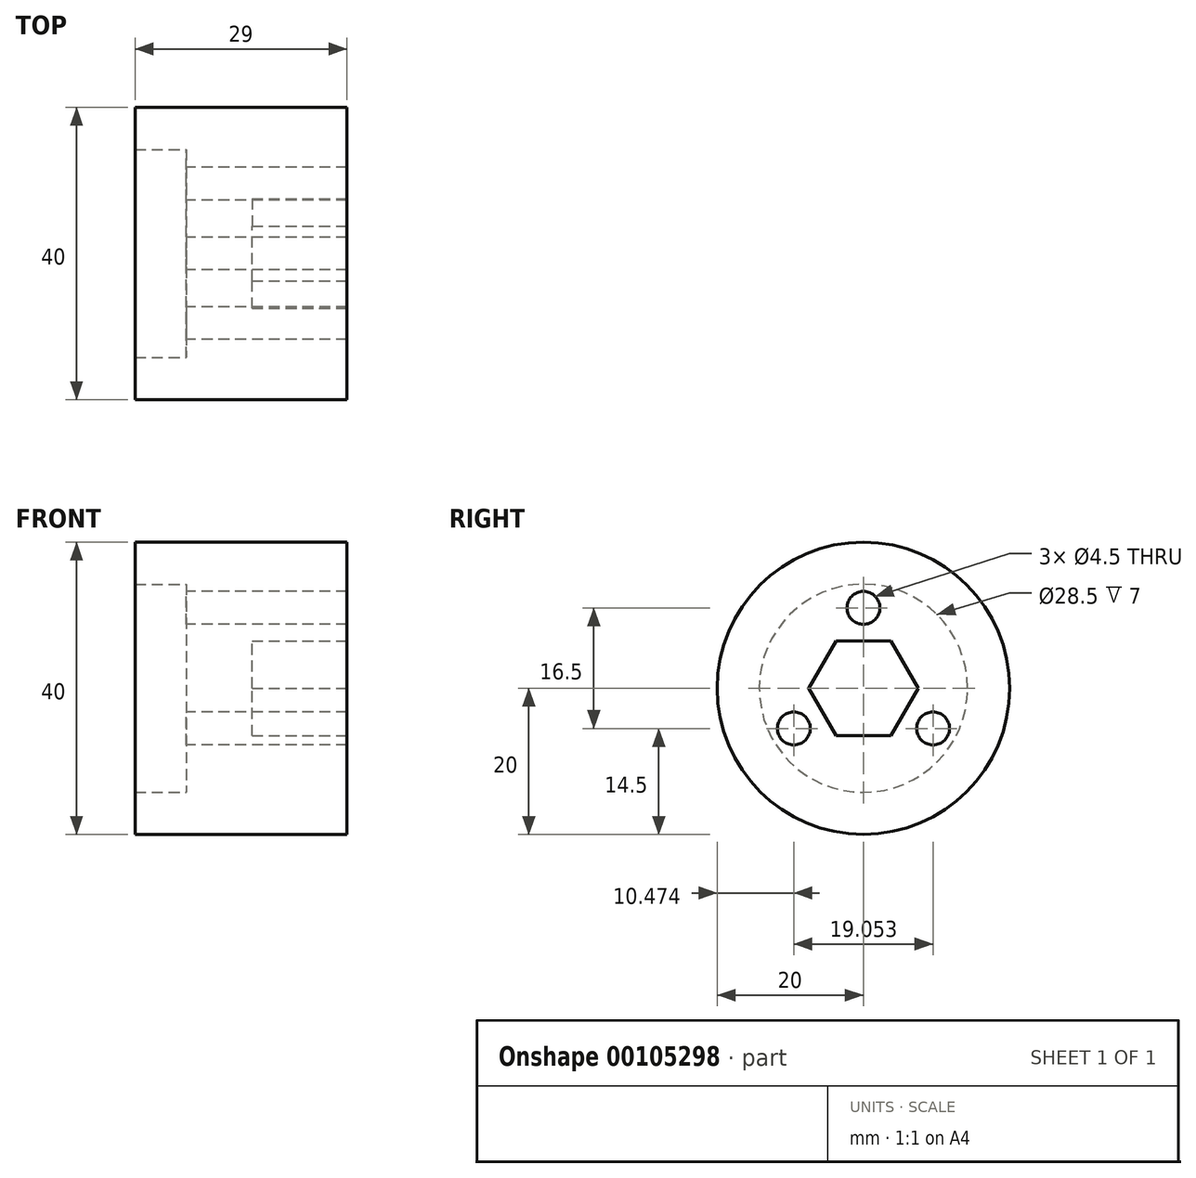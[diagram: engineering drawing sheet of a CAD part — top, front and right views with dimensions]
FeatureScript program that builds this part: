
annotation { "Feature Type Name" : "Feature", "Feature Type Description" : "" }
export const myFeature = defineFeature(function(context is Context, id is Id, definition is map)
    precondition{}
    {
        {
            var Q0;
            Q0=qCreatedBy(makeId("Right.planeOp"),FACE);
            var sketch = newSketch(context, id + "F0", { "sketchPlane" : qUnion([Q0])});
            skCircle(sketch, "E0", {"center": v(0, 0) * mm, "radius": 14.25 * mm, "construction": true});
            skCircle(sketch, "E1", {"center": v(0, 11) * mm, "radius": 2.25 * mm});
            skCircle(sketch, "E2.1.0", {"center": v(-9.53, -5.5) * mm, "radius": 2.25 * mm});
            skCircle(sketch, "E2.2.0", {"center": v(9.53, -5.5) * mm, "radius": 2.25 * mm});
            skCircle(sketch, "E3", {"center": v(0, 0) * mm, "radius": 20 * mm});
            skSolve(sketch);
        }
        {
            var Q0;
            Q0 = qSketchRegion(id + "F0", true);
            extrude(context, id + "F1", {"entities" : qUnion([Q0]), "depth" : 22 * mm});
        }
        {
            var Q0;
            Q0=makeQuery(id+"F1.opExtrude","CAP_FACE",FACE,{"disambiguationData":[OSD([sQuery(id+"F0.wireOp",EDGE,"E1"),sQuery(id+"F0.wireOp",EDGE,"E2.1.0"),sQuery(id+"F0.wireOp",EDGE,"E2.2.0"),sQuery(id+"F0.wireOp",EDGE,"E3")])],"isStart":true});
            var sketch = newSketch(context, id + "F2", { "sketchPlane" : qUnion([Q0])});
            skCircle(sketch, "E4", {"center": v(0, 0) * mm, "radius": 14.25 * mm});
            skCircle(sketch, "E5", {"center": v(0, 0) * mm, "radius": 20 * mm});
            skSolve(sketch);
        }
        {
            var Q0;
            Q0 = qSketchRegion(id + "F2", true);
            extrude(context, id + "F3", {"entities" : qUnion([Q0]), "operationType" : NewBodyOperationType.ADD, "depth" : 7 * mm});
        }
        {
            var Q0;
            Q0=makeQuery(id+"F1.opExtrude","CAP_FACE",FACE,{"disambiguationData":[OSD([sQuery(id+"F0.wireOp",EDGE,"E1"),sQuery(id+"F0.wireOp",EDGE,"E2.1.0"),sQuery(id+"F0.wireOp",EDGE,"E2.2.0"),sQuery(id+"F0.wireOp",EDGE,"E3")])],"isStart":false});
            var sketch = newSketch(context, id + "F4", { "sketchPlane" : qUnion([Q0])});
            skCircle(sketch, "E6", {"center": v(0, 0) * mm, "radius": 6.5 * mm, "construction": true});
            skLineSegment(sketch, "E7.0", {"start": v(-3.75, 6.5) * mm, "end": v(3.75, 6.5) * mm});
            skLineSegment(sketch, "E7.1", {"start": v(3.75, 6.5) * mm, "end": v(7.5, 0) * mm});
            skLineSegment(sketch, "E7.2", {"start": v(7.5, 0) * mm, "end": v(3.75, -6.5) * mm});
            skLineSegment(sketch, "E7.3", {"start": v(3.75, -6.5) * mm, "end": v(-3.75, -6.5) * mm});
            skLineSegment(sketch, "E7.4", {"start": v(-3.75, -6.5) * mm, "end": v(-7.5, 0) * mm});
            skLineSegment(sketch, "E7.5", {"start": v(-7.5, 0) * mm, "end": v(-3.75, 6.5) * mm});
            skPoint(sketch, "E7.0.midPoint", {"position": v(0, 6.5) * mm});
            skSolve(sketch);
        }
        {
            var Q0;
            Q0 = qSketchRegion(id + "F4", true);
            extrude(context, id + "F5", {"entities" : qUnion([Q0]), "operationType" : NewBodyOperationType.REMOVE, "oppositeDirection" : true, "depth" : 13 * mm});
        }
    });
